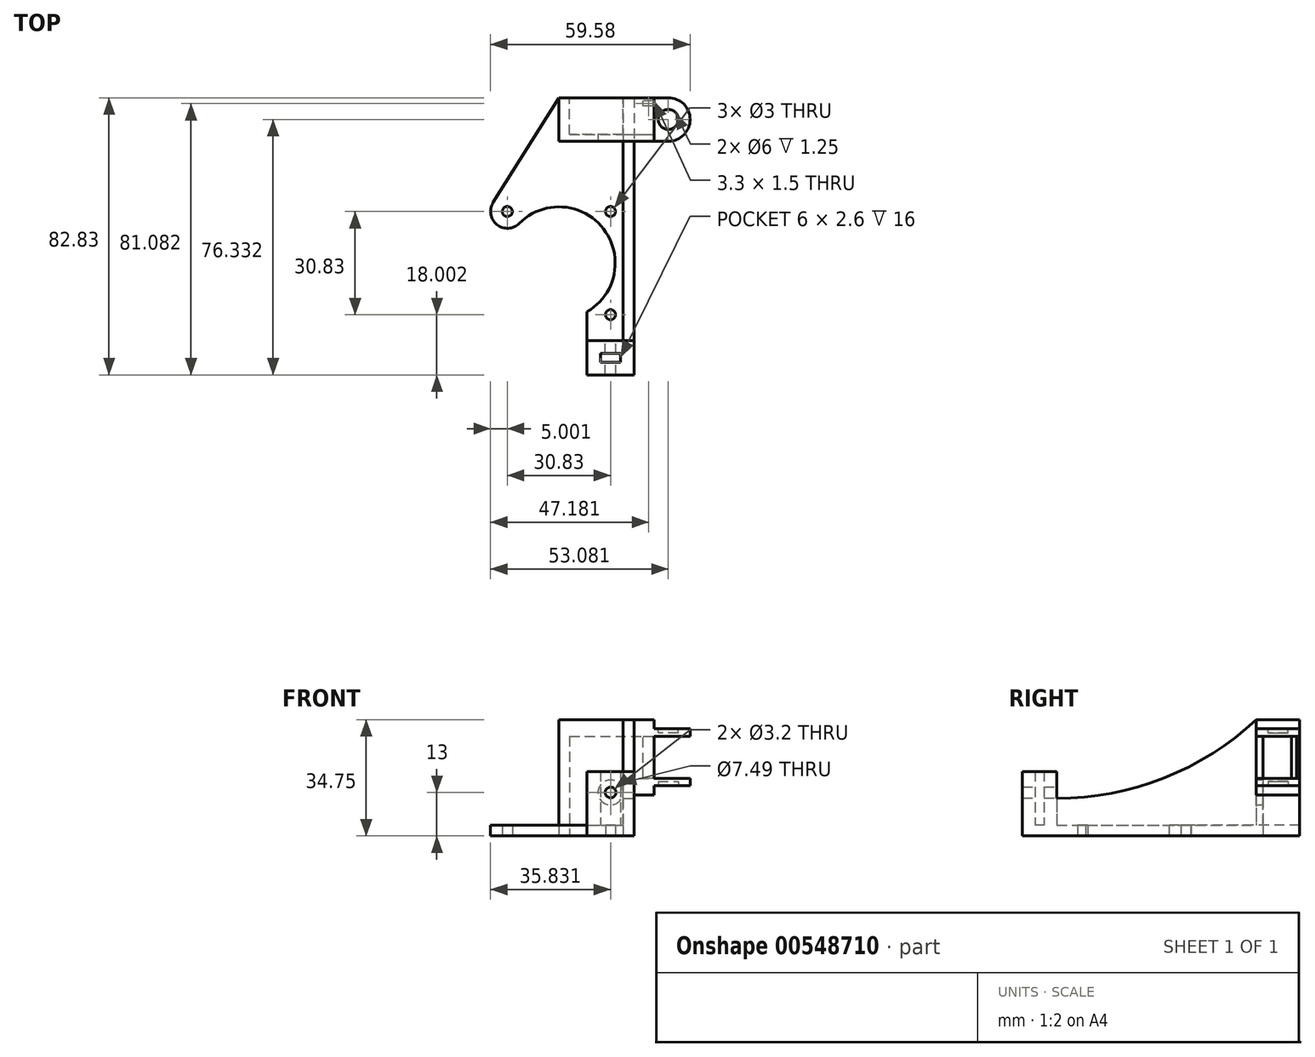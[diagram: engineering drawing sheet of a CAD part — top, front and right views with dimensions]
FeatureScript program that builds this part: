
annotation { "Feature Type Name" : "Feature", "Feature Type Description" : "" }
export const myFeature = defineFeature(function(context is Context, id is Id, definition is map)
    precondition{}
    {
        {
            var Q0;
            Q0=qCreatedBy(makeId("Top.planeOp"),FACE);
            var sketch = newSketch(context, id + "F0", { "sketchPlane" : qUnion([Q0])});
            skCircle(sketch, "E0", {"center": v(-45.23, 16.67) * mm, "radius": 1.5 * mm});
            skCircle(sketch, "E1", {"center": v(-45.23, -14.16) * mm, "radius": 1.5 * mm});
            skCircle(sketch, "E2", {"center": v(-76.06, 16.67) * mm, "radius": 1.5 * mm});
            skLineSegment(sketch, "E3", {"start": v(-52.23, -32.16) * mm, "end": v(-38.23, -32.16) * mm});
            skLineSegment(sketch, "E4", {"start": v(-52.23, -32.16) * mm, "end": v(-52.23, -13.28) * mm});
            skLineSegment(sketch, "E5", {"start": v(-38.23, -32.16) * mm, "end": v(-38.23, 50.67) * mm});
            skLineSegment(sketch, "E6", {"start": v(-38.23, 50.67) * mm, "end": v(-41.48, 50.67) * mm});
            skLineSegment(sketch, "E7", {"start": v(-41.48, 50.67) * mm, "end": v(-41.48, 39.67) * mm});
            skLineSegment(sketch, "E8", {"start": v(-41.48, 39.67) * mm, "end": v(-57.48, 39.67) * mm});
            skLineSegment(sketch, "E9", {"start": v(-57.48, 39.67) * mm, "end": v(-57.48, 50.67) * mm});
            skLineSegment(sketch, "E10", {"start": v(-57.48, 50.67) * mm, "end": v(-60.73, 50.67) * mm});
            skArc(sketch, "E11", {"start": v(-80.3, 19.32) * mm, "mid": v(-79.17, 12.76) * mm, "end": v(-72.52, 13.14) * mm});
            skLineSegment(sketch, "E12", {"start": v(-60.73, 50.67) * mm, "end": v(-80.3, 19.32) * mm});
            skLineSegment(sketch, "E13", {"start": v(-76.06, 16.67) * mm, "end": v(-45.23, -14.16) * mm, "construction": true});
            skArc(sketch, "E14", {"start": v(-52.23, -13.28) * mm, "mid": v(-47.32, 11.5) * mm, "end": v(-72.52, 13.14) * mm});
            skSolve(sketch);
        }
        {
            var Q0;
            Q0 = qSketchRegion(id + "F0", true);
            extrude(context, id + "F1", {"entities" : qUnion([Q0]), "depth" : 3.25 * mm, "offsetDistance" : 25 * mm});
        }
        {
            var Q0;
            Q0=makeQuery(id+"F1.opExtrude","CAP_FACE",FACE,{"disambiguationData":[OSD([sQuery(id+"F0.wireOp",EDGE,"E0"),sQuery(id+"F0.wireOp",EDGE,"E1"),sQuery(id+"F0.wireOp",EDGE,"E2"),sQuery(id+"F0.wireOp",EDGE,"E3"),sQuery(id+"F0.wireOp",EDGE,"E4"),sQuery(id+"F0.wireOp",EDGE,"E5"),sQuery(id+"F0.wireOp",EDGE,"E6"),sQuery(id+"F0.wireOp",EDGE,"E7"),sQuery(id+"F0.wireOp",EDGE,"E8"),sQuery(id+"F0.wireOp",EDGE,"E9"),sQuery(id+"F0.wireOp",EDGE,"E10"),sQuery(id+"F0.wireOp",EDGE,"E11"),sQuery(id+"F0.wireOp",EDGE,"E12"),sQuery(id+"F0.wireOp",EDGE,"E14")])],"isStart":false});
            var sketch = newSketch(context, id + "F2", { "sketchPlane" : qUnion([Q0])});
            skLineSegment(sketch, "E15.bottom", {"start": v(-52.23, -32.16) * mm, "end": v(-38.23, -32.16) * mm});
            skLineSegment(sketch, "E15.top", {"start": v(-52.23, -21.9) * mm, "end": v(-38.23, -21.9) * mm});
            skLineSegment(sketch, "E15.left", {"start": v(-52.23, -32.16) * mm, "end": v(-52.23, -21.9) * mm});
            skLineSegment(sketch, "E15.right", {"start": v(-38.23, -32.16) * mm, "end": v(-38.23, -21.9) * mm});
            skLineSegment(sketch, "E16.bottom", {"start": v(-48.23, -25.73) * mm, "end": v(-42.23, -25.73) * mm});
            skLineSegment(sketch, "E16.top", {"start": v(-48.23, -28.33) * mm, "end": v(-42.23, -28.33) * mm});
            skLineSegment(sketch, "E16.left", {"start": v(-48.23, -25.73) * mm, "end": v(-48.23, -28.33) * mm});
            skLineSegment(sketch, "E16.right", {"start": v(-42.23, -25.73) * mm, "end": v(-42.23, -28.33) * mm});
            skSolve(sketch);
        }
        {
            var Q0;
            Q0 = qSketchRegion(id + "F2", true);
            extrude(context, id + "F3", {"entities" : qUnion([Q0]), "operationType" : NewBodyOperationType.ADD, "depth" : 16 * mm, "offsetDistance" : 25 * mm});
        }
        {
            var Q0;
            Q0=makeQuery(id+"F3.opExtrude","SWEPT_FACE",FACE,{"disambiguationData":[OSD([sQuery(id+"F2.wireOp",EDGE,"E15.top")])]});
            var sketch = newSketch(context, id + "F4", { "sketchPlane" : qUnion([Q0])});
            skCircle(sketch, "E17", {"center": v(45.23, 13) * mm, "radius": 1.6 * mm});
            skSolve(sketch);
        }
        {
            var Q0;
            Q0 = qSketchRegion(id + "F4", true);
            extrude(context, id + "F5", {"entities" : qUnion([Q0]), "operationType" : NewBodyOperationType.REMOVE, "oppositeDirection" : true, "depth" : 25 * mm, "offsetDistance" : 25 * mm});
        }
        {
            var Q0;
            Q0=makeQuery(id+"F3.boolean.opBoolean","MERGE",FACE,{"derivedFrom":[makeQuery(id+"F1.opExtrude","SWEPT_FACE",FACE,{"disambiguationData":[OSD([sQuery(id+"F0.wireOp",EDGE,"E5")])]}),makeQuery(id+"F3.opExtrude","SWEPT_FACE",FACE,{"disambiguationData":[OSD([sQuery(id+"F2.wireOp",EDGE,"E15.right")])]})]});
            var sketch = newSketch(context, id + "F6", { "sketchPlane" : qUnion([Q0])});
            skLineSegment(sketch, "E18", {"start": v(50.67, 34.75) * mm, "end": v(37.67, 34.75) * mm});
            skArc(sketch, "E19", {"start": v(-21.9, 11.25) * mm, "mid": v(10.12, 17.34) * mm, "end": v(37.67, 34.75) * mm});
            skLineSegment(sketch, "E20", {"start": v(50.67, 3.25) * mm, "end": v(50.67, 17.25) * mm});
            skLineSegment(sketch, "E21", {"start": v(50.67, 29.75) * mm, "end": v(39.67, 29.75) * mm});
            skLineSegment(sketch, "E22", {"start": v(39.67, 29.75) * mm, "end": v(39.67, 17.25) * mm});
            skLineSegment(sketch, "E23", {"start": v(39.67, 17.25) * mm, "end": v(50.67, 17.25) * mm});
            skLineSegment(sketch, "E24", {"start": v(50.67, 3.25) * mm, "end": v(-21.9, 3.25) * mm});
            skLineSegment(sketch, "E25", {"start": v(-21.9, 3.25) * mm, "end": v(-21.9, 11.25) * mm});
            skLineSegment(sketch, "E26.trimOffspring", {"start": v(50.67, 29.75) * mm, "end": v(50.67, 34.75) * mm});
            skSolve(sketch);
        }
        {
            var Q0;
            Q0 = qSketchRegion(id + "F6", true);
            extrude(context, id + "F7", {"entities" : qUnion([Q0]), "operationType" : NewBodyOperationType.ADD, "oppositeDirection" : true, "depth" : 3.25 * mm, "offsetDistance" : 25 * mm});
        }
        {
            var Q0;
            {var subQ0=sQuery(id+"F0.wireOp",EDGE,"E10");var subQ1=sQuery(id+"F0.wireOp",EDGE,"E8");var subQ2=sQuery(id+"F0.wireOp",EDGE,"E7");var subQ3=sQuery(id+"F0.wireOp",EDGE,"E6");var subQ4=sQuery(id+"F0.wireOp",EDGE,"E5");var subQ5=sQuery(id+"F0.wireOp",EDGE,"E9");var subQ6=sQuery(id+"F0.wireOp",EDGE,"E0");var subQ7=sQuery(id+"F0.wireOp",EDGE,"E1");var subQ8=sQuery(id+"F0.wireOp",EDGE,"E2");var subQ9=sQuery(id+"F0.wireOp",EDGE,"E4");var subQ10=sQuery(id+"F0.wireOp",EDGE,"E11");var subQ11=sQuery(id+"F0.wireOp",EDGE,"E12");var subQ12=sQuery(id+"F0.wireOp",EDGE,"E14");Q0=makeQuery(id+"F3.boolean.opBoolean","SPLIT",FACE,{"disambiguationData":[TD([makeQuery(id+"F1.opExtrude","SWEPT_FACE",FACE,{"disambiguationData":[OSD([subQ6])]})])],"derivedFrom":makeQuery(id+"F1.opExtrude","CAP_FACE",FACE,{"disambiguationData":[OSD([subQ6,subQ7,subQ8,sQuery(id+"F0.wireOp",EDGE,"E3"),subQ9,subQ4,subQ3,subQ2,subQ1,subQ5,subQ0,subQ10,subQ11,subQ12])],"isStart":false})});}
            var sketch = newSketch(context, id + "F8", { "sketchPlane" : qUnion([Q0])});
            skLineSegment(sketch, "E27", {"start": v(-60.73, 50.67) * mm, "end": v(-60.73, 37.67) * mm});
            skLineSegment(sketch, "E28", {"start": v(-60.73, 37.67) * mm, "end": v(-41.48, 37.67) * mm});
            skLineSegment(sketch, "E29", {"start": v(-41.48, 37.67) * mm, "end": v(-41.48, 39.67) * mm});
            skLineSegment(sketch, "E30", {"start": v(-41.48, 39.67) * mm, "end": v(-57.48, 39.67) * mm});
            skLineSegment(sketch, "E31", {"start": v(-57.48, 39.67) * mm, "end": v(-57.48, 50.67) * mm});
            skLineSegment(sketch, "E32", {"start": v(-57.48, 50.67) * mm, "end": v(-60.73, 50.67) * mm});
            skSolve(sketch);
        }
        {
            var Q0;
            Q0=makeQuery(id+"F8.imprint","IMPRINT",FACE,{"disambiguationData":[TD([[makeQuery(id+"F8.imprint","IMPRINT",EDGE,{"derivedFrom":sQuery(id+"F8.wireOp",EDGE,"E27")}),1.0]])]});
            extrude(context, id + "F9", {"entities" : qUnion([Q0]), "operationType" : NewBodyOperationType.ADD, "depth" : 31.5 * mm, "offsetDistance" : 25 * mm});
        }
        {
            var Q0;
            Q0=makeQuery(id+"F9.boolean.opBoolean","MERGE",FACE,{"derivedFrom":[makeQuery(id+"F7.opExtrude","SWEPT_FACE",FACE,{"disambiguationData":[OSD([sQuery(id+"F6.wireOp",EDGE,"E18")])]}),makeQuery(id+"F9.opExtrude","CAP_FACE",FACE,{"disambiguationData":[OSD([sQuery(id+"F6.wireOp",EDGE,"E24"),sQuery(id+"F8.wireOp",EDGE,"E27"),sQuery(id+"F8.wireOp",EDGE,"E28"),sQuery(id+"F8.wireOp",EDGE,"E30"),sQuery(id+"F8.wireOp",EDGE,"E31"),sQuery(id+"F8.wireOp",EDGE,"E32")])],"isStart":false})]});
            var sketch = newSketch(context, id + "F10", { "sketchPlane" : qUnion([Q0])});
            skLineSegment(sketch, "E33.bottom", {"start": v(-57.48, 50.67) * mm, "end": v(-41.48, 50.67) * mm});
            skLineSegment(sketch, "E33.top", {"start": v(-57.48, 39.67) * mm, "end": v(-41.48, 39.67) * mm});
            skLineSegment(sketch, "E33.left", {"start": v(-57.48, 50.67) * mm, "end": v(-57.48, 39.67) * mm});
            skLineSegment(sketch, "E33.right", {"start": v(-41.48, 50.67) * mm, "end": v(-41.48, 39.67) * mm});
            skSolve(sketch);
        }
        {
            var Q0;
            Q0 = qSketchRegion(id + "F10", true);
            extrude(context, id + "F11", {"entities" : qUnion([Q0]), "operationType" : NewBodyOperationType.ADD, "oppositeDirection" : true, "depth" : 5 * mm, "offsetDistance" : 25 * mm});
        }
        {
            var Q0;
            Q0=makeQuery(id+"F7.boolean.opBoolean","MERGE",FACE,{"derivedFrom":[makeQuery(id+"F3.boolean.opBoolean","MERGE",FACE,{"derivedFrom":[makeQuery(id+"F1.opExtrude","SWEPT_FACE",FACE,{"disambiguationData":[OSD([sQuery(id+"F0.wireOp",EDGE,"E5")])]}),makeQuery(id+"F3.opExtrude","SWEPT_FACE",FACE,{"disambiguationData":[OSD([sQuery(id+"F2.wireOp",EDGE,"E15.right")])]})]}),makeQuery(id+"F7.opExtrude","CAP_FACE",FACE,{"disambiguationData":[OSD([sQuery(id+"F6.wireOp",EDGE,"E18"),sQuery(id+"F6.wireOp",EDGE,"E19"),sQuery(id+"F6.wireOp",EDGE,"E20"),sQuery(id+"F6.wireOp",EDGE,"E21"),sQuery(id+"F6.wireOp",EDGE,"E22"),sQuery(id+"F6.wireOp",EDGE,"E23"),sQuery(id+"F6.wireOp",EDGE,"E24"),sQuery(id+"F6.wireOp",EDGE,"E25"),sQuery(id+"F6.wireOp",EDGE,"E26.trimOffspring")])],"isStart":true})]});
            var sketch = newSketch(context, id + "F12", { "sketchPlane" : qUnion([Q0])});
            skLineSegment(sketch, "E34.bottom", {"start": v(50.67, 29.75) * mm, "end": v(39.67, 29.75) * mm});
            skLineSegment(sketch, "E34.top", {"start": v(50.67, 34.75) * mm, "end": v(37.67, 34.75) * mm});
            skLineSegment(sketch, "E34.left", {"start": v(50.67, 29.75) * mm, "end": v(50.67, 34.75) * mm});
            skLineSegment(sketch, "E34.right", {"start": v(37.67, 12.25) * mm, "end": v(37.67, 34.75) * mm});
            skLineSegment(sketch, "E35.bottom", {"start": v(50.67, 17.25) * mm, "end": v(39.67, 17.25) * mm});
            skLineSegment(sketch, "E35.top", {"start": v(50.67, 12.25) * mm, "end": v(37.67, 12.25) * mm});
            skLineSegment(sketch, "E35.left", {"start": v(50.67, 17.25) * mm, "end": v(50.67, 12.25) * mm});
            skLineSegment(sketch, "E36.left", {"start": v(39.67, 29.75) * mm, "end": v(39.67, 17.25) * mm});
            skSolve(sketch);
        }
        {
            var Q0;
            Q0=makeQuery(id+"F12.imprint","IMPRINT",FACE,{"disambiguationData":[TD([[makeQuery(id+"F12.imprint","IMPRINT",EDGE,{"derivedFrom":sQuery(id+"F12.wireOp",EDGE,"E34.bottom")}),-1.0]])]});
            extrude(context, id + "F13", {"entities" : qUnion([Q0]), "operationType" : NewBodyOperationType.ADD, "depth" : 6 * mm, "offsetDistance" : 25 * mm});
        }
        {
            var Q0;
            Q0=makeQuery(id+"F13.opExtrude","CAP_FACE",FACE,{"disambiguationData":[OSD([sQuery(id+"F12.wireOp",EDGE,"E34.bottom"),sQuery(id+"F12.wireOp",EDGE,"E34.top"),sQuery(id+"F12.wireOp",EDGE,"E34.left"),sQuery(id+"F12.wireOp",EDGE,"E34.right"),sQuery(id+"F12.wireOp",EDGE,"E35.bottom"),sQuery(id+"F12.wireOp",EDGE,"E35.top"),sQuery(id+"F12.wireOp",EDGE,"E35.left"),sQuery(id+"F12.wireOp",EDGE,"E36.left")])],"isStart":false});
            var sketch = newSketch(context, id + "F14", { "sketchPlane" : qUnion([Q0])});
            skPoint(sketch, "E37.oppositeSnap0", {"position": v(50.67, 32.25) * mm});
            skLineSegment(sketch, "E37.bottom", {"start": v(50.67, 29.75) * mm, "end": v(37.67, 29.75) * mm});
            skLineSegment(sketch, "E37.left", {"start": v(50.67, 29.75) * mm, "end": v(50.67, 32) * mm});
            skLineSegment(sketch, "E37.right", {"start": v(37.67, 29.75) * mm, "end": v(37.67, 32) * mm});
            skLineSegment(sketch, "E38.bottom", {"start": v(50.67, 17.25) * mm, "end": v(37.67, 17.25) * mm});
            skLineSegment(sketch, "E38.top", {"start": v(50.67, 15) * mm, "end": v(37.67, 15) * mm});
            skLineSegment(sketch, "E38.left", {"start": v(50.67, 17.25) * mm, "end": v(50.67, 15) * mm});
            skLineSegment(sketch, "E38.right", {"start": v(37.67, 17.25) * mm, "end": v(37.67, 15) * mm});
            skLineSegment(sketch, "E39", {"start": v(50.67, 32) * mm, "end": v(37.67, 32) * mm});
            skPoint(sketch, "E40.orphan", {"position": v(37.67, 32.25) * mm});
            skSolve(sketch);
        }
        {
            var Q0;
            {var subQ1=sQuery(id+"F14.wireOp",EDGE,"E37.left");Q0=makeQuery(id+"F14.imprint","IMPRINT",FACE,{"disambiguationData":[TD([[makeQuery(id+"F14.imprint","IMPRINT",EDGE,{"derivedFrom":subQ1}),1.0]])]});}
            var Q1;
            Q1=makeQuery(id+"F14.imprint","IMPRINT",FACE,{"disambiguationData":[TD([[makeQuery(id+"F14.imprint","IMPRINT",EDGE,{"derivedFrom":sQuery(id+"F14.wireOp",EDGE,"E38.top")}),-1.0]])]});
            extrude(context, id + "F15", {"entities" : qUnion([Q0, Q1]), "operationType" : NewBodyOperationType.ADD, "depth" : 10.75 * mm, "offsetDistance" : 25 * mm});
        }
        {
            var Q0;
            Q0=makeQuery(id+"F15.opExtrude","CAP_EDGE",EDGE,{"disambiguationData":[OSD([sQuery(id+"F14.wireOp",EDGE,"E37.left")])],"isStart":false});
            var Q1;
            Q1=makeQuery(id+"F15.opExtrude","CAP_EDGE",EDGE,{"disambiguationData":[OSD([sQuery(id+"F12.wireOp",EDGE,"E35.left")])],"isStart":false});
            var Q2;
            Q2=makeQuery(id+"F15.opExtrude","CAP_EDGE",EDGE,{"disambiguationData":[OSD([sQuery(id+"F12.wireOp",EDGE,"E34.right")])],"isStart":false});
            var Q3;
            Q3=makeQuery(id+"F15.opExtrude","CAP_EDGE",EDGE,{"disambiguationData":[OSD([sQuery(id+"F14.wireOp",EDGE,"E37.right")])],"isStart":false});
            fillet(context, id + "F16", {"entities" : qUnion([Q0, Q1, Q2, Q3]), "radius" : 6.5 * mm, "tangentPropagation" : true, "allowEdgeOverflow" : false});
        }
        {
            var Q0;
            Q0=makeQuery(id+"F15.opExtrude","SWEPT_FACE",FACE,{"disambiguationData":[OSD([sQuery(id+"F14.wireOp",EDGE,"E39")])]});
            var sketch = newSketch(context, id + "F17", { "sketchPlane" : qUnion([Q0])});
            skCircle(sketch, "E41", {"center": v(-27.98, 44.17) * mm, "radius": 3 * mm});
            skSolve(sketch);
        }
        {
            var Q0;
            Q0 = qSketchRegion(id + "F17", true);
            extrude(context, id + "F18", {"entities" : qUnion([Q0]), "operationType" : NewBodyOperationType.REMOVE, "oppositeDirection" : true, "depth" : 1.25 * mm, "offsetDistance" : 25 * mm});
        }
        {
            var Q0;
            Q0=makeQuery(id+"F15.opExtrude","CAP_EDGE",EDGE,{"disambiguationData":[OSD([sQuery(id+"F14.wireOp",EDGE,"E38.left")])],"isStart":false});
            var Q1;
            Q1=makeQuery(id+"F15.opExtrude","CAP_EDGE",EDGE,{"disambiguationData":[OSD([sQuery(id+"F14.wireOp",EDGE,"E38.right")])],"isStart":false});
            fillet(context, id + "F19", {"entities" : qUnion([Q0, Q1]), "radius" : 6.5 * mm, "tangentPropagation" : true, "allowEdgeOverflow" : false});
        }
        {
            var Q0;
            Q0=makeQuery(id+"F15.opExtrude","SWEPT_FACE",FACE,{"disambiguationData":[OSD([sQuery(id+"F14.wireOp",EDGE,"E38.top")])]});
            var sketch = newSketch(context, id + "F20", { "sketchPlane" : qUnion([Q0])});
            skCircle(sketch, "E42", {"center": v(-27.98, -44.17) * mm, "radius": 3 * mm});
            skSolve(sketch);
        }
        {
            var Q0;
            Q0 = qSketchRegion(id + "F20", true);
            extrude(context, id + "F21", {"entities" : qUnion([Q0]), "operationType" : NewBodyOperationType.REMOVE, "oppositeDirection" : true, "depth" : 1.25 * mm, "offsetDistance" : 25 * mm});
        }
        {
            var Q0;
            Q0=makeQuery(id+"F9.opExtrude","SWEPT_FACE",FACE,{"disambiguationData":[OSD([sQuery(id+"F8.wireOp",EDGE,"E28")])]});
            var sketch = newSketch(context, id + "F22", { "sketchPlane" : qUnion([Q0])});
            skCircle(sketch, "E43", {"center": v(-45.23, 13) * mm, "radius": 3.75 * mm});
            skSolve(sketch);
        }
        {
            var Q0;
            Q0=makeQuery(id+"F22.imprint","IMPRINT",FACE,{"disambiguationData":[TD([[makeQuery(id+"F22.imprint","IMPRINT",EDGE,{"derivedFrom":sQuery(id+"F22.wireOp",EDGE,"E43")}),1.0]])]});
            extrude(context, id + "F23", {"entities" : qUnion([Q0]), "operationType" : NewBodyOperationType.REMOVE, "oppositeDirection" : true, "depth" : 25 * mm, "offsetDistance" : 25 * mm});
        }
        {
            var Q0;
            Q0=makeQuery(id+"F13.boolean.opBoolean","MERGE",FACE,{"derivedFrom":[makeQuery(id+"F11.boolean.opBoolean","MERGE",FACE,{"derivedFrom":[makeQuery(id+"F9.boolean.opBoolean","MERGE",FACE,{"derivedFrom":[makeQuery(id+"F7.opExtrude","SWEPT_FACE",FACE,{"disambiguationData":[OSD([sQuery(id+"F6.wireOp",EDGE,"E18")])]}),makeQuery(id+"F9.opExtrude","CAP_FACE",FACE,{"disambiguationData":[OSD([sQuery(id+"F6.wireOp",EDGE,"E24"),sQuery(id+"F8.wireOp",EDGE,"E27"),sQuery(id+"F8.wireOp",EDGE,"E28"),sQuery(id+"F8.wireOp",EDGE,"E30"),sQuery(id+"F8.wireOp",EDGE,"E31"),sQuery(id+"F8.wireOp",EDGE,"E32")])],"isStart":false})]}),makeQuery(id+"F11.opExtrude","CAP_FACE",FACE,{"disambiguationData":[OSD([sQuery(id+"F10.wireOp",EDGE,"E33.bottom"),sQuery(id+"F10.wireOp",EDGE,"E33.top"),sQuery(id+"F10.wireOp",EDGE,"E33.left"),sQuery(id+"F10.wireOp",EDGE,"E33.right")])],"isStart":true})]}),makeQuery(id+"F13.opExtrude","SWEPT_FACE",FACE,{"disambiguationData":[OSD([sQuery(id+"F12.wireOp",EDGE,"E34.top")])]})]});
            var sketch = newSketch(context, id + "F24", { "sketchPlane" : qUnion([Q0])});
            skLineSegment(sketch, "E44.bottom", {"start": v(-35.53, 49.67) * mm, "end": v(-32.23, 49.67) * mm});
            skLineSegment(sketch, "E44.top", {"start": v(-35.53, 48.17) * mm, "end": v(-32.23, 48.17) * mm});
            skLineSegment(sketch, "E44.left", {"start": v(-35.53, 49.67) * mm, "end": v(-35.53, 48.17) * mm});
            skLineSegment(sketch, "E44.right", {"start": v(-32.23, 49.67) * mm, "end": v(-32.23, 48.17) * mm});
            skSolve(sketch);
        }
        {
            var Q0;
            Q0 = qSketchRegion(id + "F24", true);
            extrude(context, id + "F25", {"entities" : qUnion([Q0]), "operationType" : NewBodyOperationType.ADD, "oppositeDirection" : true, "depth" : 20 * mm, "offsetDistance" : 25 * mm});
        }
    });
